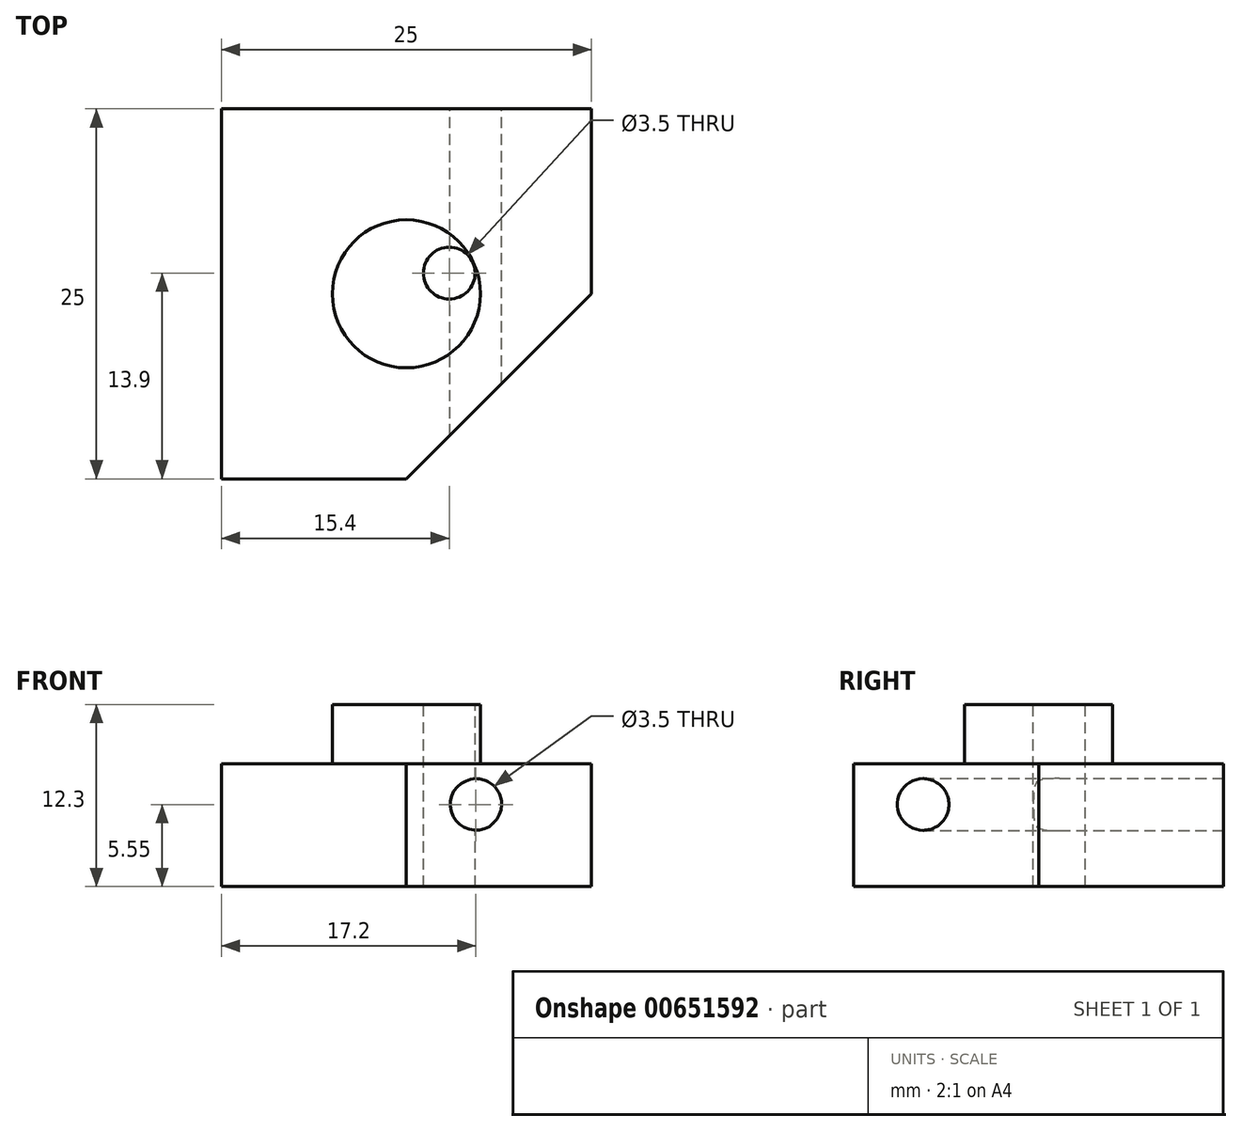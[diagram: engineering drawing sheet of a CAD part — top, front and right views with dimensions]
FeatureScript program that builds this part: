
annotation { "Feature Type Name" : "Feature", "Feature Type Description" : "" }
export const myFeature = defineFeature(function(context is Context, id is Id, definition is map)
    precondition{}
    {
        {
            var Q0;
            Q0=qCreatedBy(makeId("Top.planeOp"),FACE);
            var sketch = newSketch(context, id + "F0", { "sketchPlane" : qUnion([Q0])});
            skLineSegment(sketch, "E0.bottom", {"start": v(12.5, 12.5) * mm, "end": v(-12.5, 12.5) * mm});
            skLineSegment(sketch, "E0.top", {"start": v(12.5, -12.5) * mm, "end": v(-12.5, -12.5) * mm});
            skLineSegment(sketch, "E0.left", {"start": v(12.5, 12.5) * mm, "end": v(12.5, -12.5) * mm});
            skLineSegment(sketch, "E0.right", {"start": v(-12.5, 12.5) * mm, "end": v(-12.5, -12.5) * mm});
            skPoint(sketch, "E0.middle", {"position": v(0, 0) * mm});
            skSolve(sketch);
        }
        {
            var Q0;
            Q0=makeQuery(id+"F0.imprint","IMPRINT",FACE,{"disambiguationData":[TD([[makeQuery(id+"F0.imprint","IMPRINT",EDGE,{"derivedFrom":sQuery(id+"F0.wireOp",EDGE,"E0.bottom")}),1.0]])]});
            extrude(context, id + "F1", {"entities" : qUnion([Q0]), "depth" : 8.3 * mm});
        }
        {
            var Q0;
            Q0=makeQuery(id+"F1.opExtrude","CAP_FACE",FACE,{"disambiguationData":[OSD([sQuery(id+"F0.wireOp",EDGE,"E0.bottom"),sQuery(id+"F0.wireOp",EDGE,"E0.top"),sQuery(id+"F0.wireOp",EDGE,"E0.left"),sQuery(id+"F0.wireOp",EDGE,"E0.right")])],"isStart":false});
            var sketch = newSketch(context, id + "F2", { "sketchPlane" : qUnion([Q0])});
            skCircle(sketch, "E1", {"center": v(0, 0) * mm, "radius": 5 * mm});
            skSolve(sketch);
        }
        {
            var Q0;
            Q0=makeQuery(id+"F2.imprint","IMPRINT",FACE,{"disambiguationData":[TD([[makeQuery(id+"F2.imprint","IMPRINT",EDGE,{"derivedFrom":sQuery(id+"F2.wireOp",EDGE,"E1")}),1.0]])]});
            extrude(context, id + "F3", {"entities" : qUnion([Q0]), "operationType" : NewBodyOperationType.ADD, "depth" : 4 * mm});
        }
        {
            var Q0;
            Q0=makeQuery(id+"F1.opExtrude","CAP_FACE",FACE,{"disambiguationData":[OSD([sQuery(id+"F0.wireOp",EDGE,"E0.bottom"),sQuery(id+"F0.wireOp",EDGE,"E0.top"),sQuery(id+"F0.wireOp",EDGE,"E0.left"),sQuery(id+"F0.wireOp",EDGE,"E0.right")])],"isStart":false});
            var sketch = newSketch(context, id + "F4", { "sketchPlane" : qUnion([Q0])});
            skLineSegment(sketch, "E2", {"start": v(12.5, 0) * mm, "end": v(0, -12.5) * mm});
            skLineSegment(sketch, "E3", {"start": v(0, -12.5) * mm, "end": v(12.5, -12.5) * mm});
            skLineSegment(sketch, "E4", {"start": v(12.5, -12.5) * mm, "end": v(12.5, 0) * mm});
            skSolve(sketch);
        }
        {
            var Q0;
            Q0=makeQuery(id+"F4.imprint","IMPRINT",FACE,{"disambiguationData":[TD([[makeQuery(id+"F4.imprint","IMPRINT",EDGE,{"derivedFrom":sQuery(id+"F4.wireOp",EDGE,"E2")}),1.0]])]});
            extrude(context, id + "F5", {"entities" : qUnion([Q0]), "operationType" : NewBodyOperationType.REMOVE, "oppositeDirection" : true, "depth" : 25 * mm});
        }
        {
            var Q0;
            Q0=makeQuery(id+"F3.opExtrude","CAP_FACE",FACE,{"disambiguationData":[OSD([sQuery(id+"F2.wireOp",EDGE,"E1")])],"isStart":false});
            var sketch = newSketch(context, id + "F6", { "sketchPlane" : qUnion([Q0])});
            skLineSegment(sketch, "E5", {"start": v(0, 0) * mm, "end": v(5, 0) * mm, "construction": true});
            skLineSegment(sketch, "E6", {"start": v(0, 0) * mm, "end": v(2.9, 1.4) * mm, "construction": true});
            skCircle(sketch, "E7", {"center": v(2.9, 1.4) * mm, "radius": 1.75 * mm});
            skLineSegment(sketch, "E8", {"start": v(2.9, 1.4) * mm, "end": v(-12.5, 1.4) * mm, "construction": true});
            skLineSegment(sketch, "E9", {"start": v(2.9, 1.4) * mm, "end": v(2.9, 12.5) * mm, "construction": true});
            skSolve(sketch);
        }
        {
            var Q0;
            Q0=makeQuery(id+"F6.imprint","IMPRINT",FACE,{"disambiguationData":[TD([[makeQuery(id+"F6.imprint","IMPRINT",EDGE,{"derivedFrom":sQuery(id+"F6.wireOp",EDGE,"E7")}),1.0]])]});
            extrude(context, id + "F7", {"entities" : qUnion([Q0]), "operationType" : NewBodyOperationType.REMOVE, "oppositeDirection" : true, "depth" : 25 * mm});
        }
        {
            var Q0;
            Q0=makeQuery(id+"F1.opExtrude","SWEPT_FACE",FACE,{"disambiguationData":[OSD([sQuery(id+"F0.wireOp",EDGE,"E0.bottom")])]});
            var sketch = newSketch(context, id + "F8", { "sketchPlane" : qUnion([Q0])});
            skLineSegment(sketch, "E10", {"start": v(-12.5, 5.55) * mm, "end": v(-4.7, 5.55) * mm, "construction": true});
            skCircle(sketch, "E11", {"center": v(-4.7, 5.55) * mm, "radius": 1.75 * mm});
            skLineSegment(sketch, "E12", {"start": v(-4.7, 5.55) * mm, "end": v(-4.7, 8.3) * mm});
            skSolve(sketch);
        }
        {
            var Q0;
            Q0=makeQuery(id+"F8.imprint","IMPRINT",FACE,{"disambiguationData":[TD([[makeQuery(id+"F8.imprint","IMPRINT",EDGE,{"derivedFrom":sQuery(id+"F8.wireOp",EDGE,"E11")}),1.0]])]});
            extrude(context, id + "F9", {"entities" : qUnion([Q0]), "operationType" : NewBodyOperationType.REMOVE, "oppositeDirection" : true, "depth" : 25 * mm});
        }
    });
